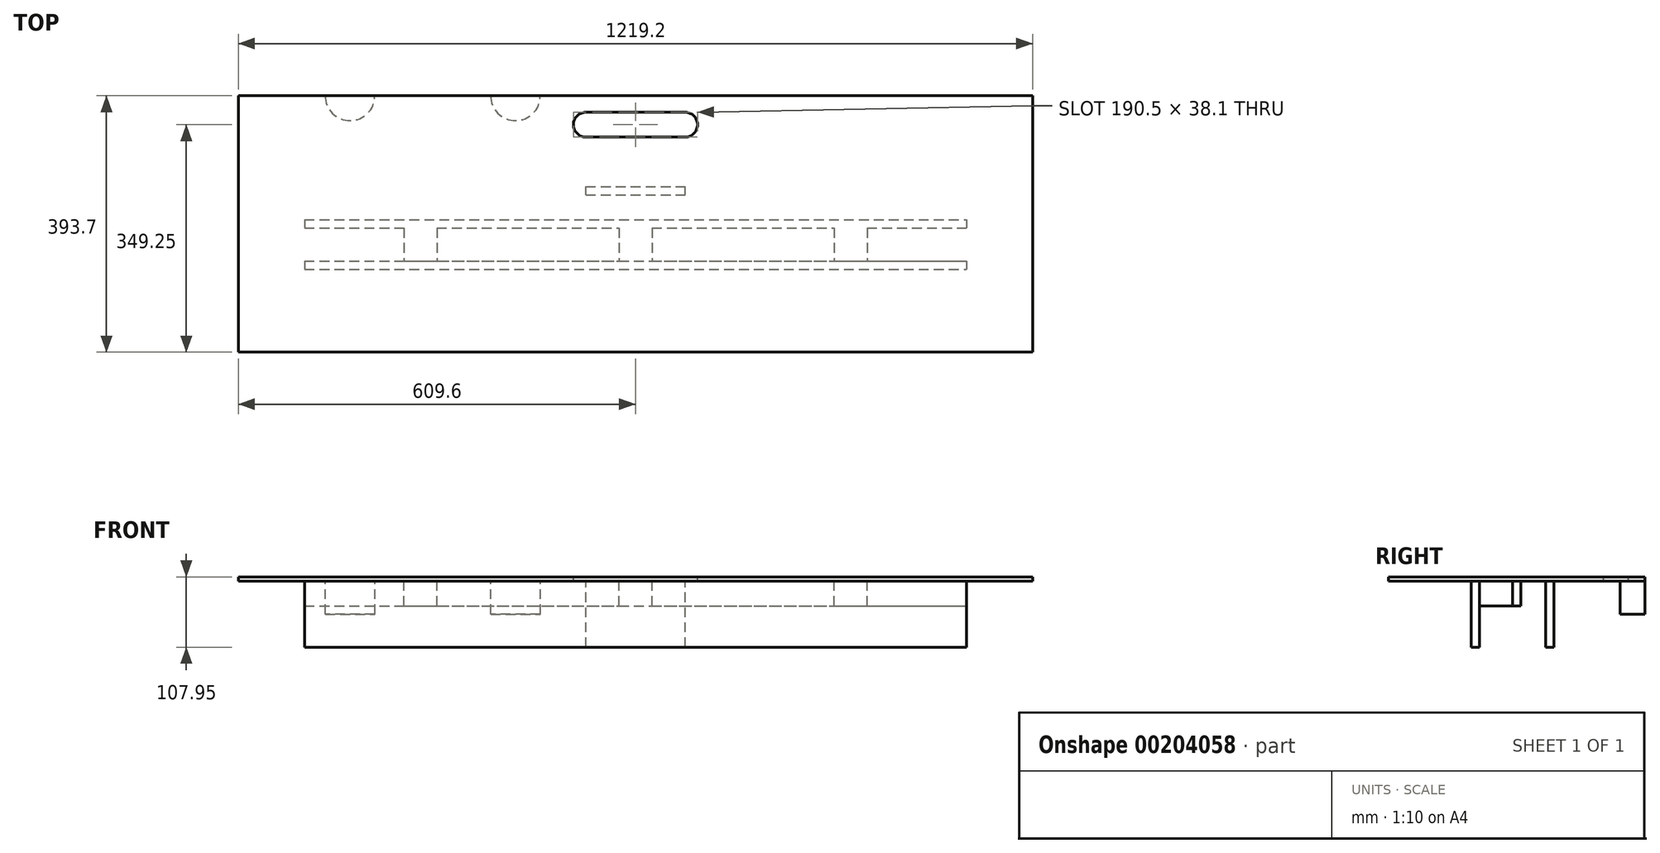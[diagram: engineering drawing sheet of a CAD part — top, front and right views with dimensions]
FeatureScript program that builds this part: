
annotation { "Feature Type Name" : "Feature", "Feature Type Description" : "" }
export const myFeature = defineFeature(function(context is Context, id is Id, definition is map)
    precondition{}
    {
        {
            var Q0;
            Q0=qCreatedBy(makeId("Top.planeOp"),FACE);
            var sketch = newSketch(context, id + "F0", { "sketchPlane" : qUnion([Q0])});
            skLineSegment(sketch, "E0.bottom", {"start": v(0, 0) * mm, "end": v(1219.2, 0) * mm});
            skLineSegment(sketch, "E0.top", {"start": v(0, 393.7) * mm, "end": v(1219.2, 393.7) * mm});
            skLineSegment(sketch, "E0.left", {"start": v(0, 0) * mm, "end": v(0, 393.7) * mm});
            skLineSegment(sketch, "E0.right", {"start": v(1219.2, 0) * mm, "end": v(1219.2, 393.7) * mm});
            skSolve(sketch);
        }
        {
            var Q0;
            Q0=makeQuery(id+"F0.imprint","IMPRINT",FACE,{"disambiguationData":[TD([[makeQuery(id+"F0.imprint","IMPRINT",EDGE,{"derivedFrom":sQuery(id+"F0.wireOp",EDGE,"E0.bottom")}),1.0]])]});
            extrude(context, id + "F1", {"entities" : qUnion([Q0]), "depth" : 6.35 * mm});
        }
        {
            var Q0;
            Q0=makeQuery(id+"F1.opExtrude","CAP_FACE",FACE,{"disambiguationData":[OSD([sQuery(id+"F0.wireOp",EDGE,"E0.bottom"),sQuery(id+"F0.wireOp",EDGE,"E0.top"),sQuery(id+"F0.wireOp",EDGE,"E0.left"),sQuery(id+"F0.wireOp",EDGE,"E0.right")])],"isStart":false});
            var sketch = newSketch(context, id + "F2", { "sketchPlane" : qUnion([Q0])});
            skLineSegment(sketch, "E1", {"start": v(533.4, 349.25) * mm, "end": v(685.8, 349.25) * mm});
            skLineSegment(sketch, "E2.0.0", {"start": v(0, 393.7) * mm, "end": v(0, 0) * mm});
            skLineSegment(sketch, "E2.0.1", {"start": v(0, 0) * mm, "end": v(1219.2, 0) * mm});
            skLineSegment(sketch, "E2.0.2", {"start": v(1219.2, 0) * mm, "end": v(1219.2, 393.7) * mm});
            skLineSegment(sketch, "E2.0.3", {"start": v(1219.2, 393.7) * mm, "end": v(0, 393.7) * mm});
            skLineSegment(sketch, "E3", {"start": v(609.6, 393.7) * mm, "end": v(609.6, 0) * mm, "construction": true});
            skCircle(sketch, "E4", {"center": v(533.4, 349.25) * mm, "radius": 19.05 * mm});
            skCircle(sketch, "E5", {"center": v(685.8, 349.25) * mm, "radius": 19.05 * mm});
            skLineSegment(sketch, "E6", {"start": v(533.4, 368.3) * mm, "end": v(685.8, 368.3) * mm});
            skLineSegment(sketch, "E7", {"start": v(685.8, 330.2) * mm, "end": v(533.4, 330.2) * mm});
            skSolve(sketch);
        }
        {
            var Q0;
            {var subQ0=sQuery(id+"F2.wireOp",EDGE,"E4");var subQ1=makeQuery(id+"F2.imprint","INTERSECT",VERTEX,{"derivedFrom":[subQ0,sQuery(id+"F2.wireOp",EDGE,"E6")]});Q0=makeQuery(id+"F2.imprint","IMPRINT",FACE,{"disambiguationData":[TD([[makeQuery(id+"F2.imprint","IMPRINT",EDGE,{"disambiguationData":[TD([[subQ1,1.0]])],"derivedFrom":subQ0}),1.0]])]});}
            var Q1;
            {var subQ5=sQuery(id+"F2.wireOp",EDGE,"E6");Q1=makeQuery(id+"F2.imprint","IMPRINT",FACE,{"disambiguationData":[TD([[makeQuery(id+"F2.imprint","IMPRINT",EDGE,{"derivedFrom":subQ5}),-1.0]])]});}
            var Q2;
            {var subQ5=sQuery(id+"F2.wireOp",EDGE,"E7");Q2=makeQuery(id+"F2.imprint","IMPRINT",FACE,{"disambiguationData":[TD([[makeQuery(id+"F2.imprint","IMPRINT",EDGE,{"derivedFrom":subQ5}),-1.0]])]});}
            var Q3;
            {var subQ0=sQuery(id+"F2.wireOp",EDGE,"E5");var subQ1=makeQuery(id+"F2.imprint","INTERSECT",VERTEX,{"derivedFrom":[subQ0,sQuery(id+"F2.wireOp",EDGE,"E6")]});Q3=makeQuery(id+"F2.imprint","IMPRINT",FACE,{"disambiguationData":[TD([[makeQuery(id+"F2.imprint","IMPRINT",EDGE,{"disambiguationData":[TD([[subQ1,-1.0]])],"derivedFrom":subQ0}),1.0]])]});}
            extrude(context, id + "F3", {"entities" : qUnion([Q0, Q1, Q2, Q3]), "operationType" : NewBodyOperationType.REMOVE, "endBound" : BoundingType.THROUGH_ALL, "oppositeDirection" : true, "depth" : 25.4 * mm});
        }
        {
            var Q0;
            Q0=makeQuery(id+"F1.opExtrude","CAP_FACE",FACE,{"disambiguationData":[OSD([sQuery(id+"F0.wireOp",EDGE,"E0.bottom"),sQuery(id+"F0.wireOp",EDGE,"E0.top"),sQuery(id+"F0.wireOp",EDGE,"E0.left"),sQuery(id+"F0.wireOp",EDGE,"E0.right")])],"isStart":true});
            var sketch = newSketch(context, id + "F4", { "sketchPlane" : qUnion([Q0])});
            skLineSegment(sketch, "E8.0.0", {"start": v(0, 0) * mm, "end": v(0, -393.7) * mm});
            skLineSegment(sketch, "E8.0.1", {"start": v(0, -393.7) * mm, "end": v(1219.2, -393.7) * mm});
            skLineSegment(sketch, "E8.0.2", {"start": v(1219.2, -393.7) * mm, "end": v(1219.2, 0) * mm});
            skLineSegment(sketch, "E8.0.3", {"start": v(1219.2, 0) * mm, "end": v(0, 0) * mm});
            skLineSegment(sketch, "E9", {"start": v(609.6, -393.7) * mm, "end": v(609.6, 0) * mm, "construction": true});
            skLineSegment(sketch, "E10.bottom", {"start": v(533.4, -241.3) * mm, "end": v(685.8, -241.3) * mm});
            skLineSegment(sketch, "E10.top", {"start": v(533.4, -254) * mm, "end": v(685.8, -254) * mm});
            skLineSegment(sketch, "E10.left", {"start": v(533.4, -241.3) * mm, "end": v(533.4, -254) * mm});
            skLineSegment(sketch, "E10.right", {"start": v(685.8, -241.3) * mm, "end": v(685.8, -254) * mm});
            skSolve(sketch);
        }
        {
            var Q0;
            Q0=makeQuery(id+"F4.imprint","IMPRINT",FACE,{"disambiguationData":[TD([[makeQuery(id+"F4.imprint","IMPRINT",EDGE,{"derivedFrom":sQuery(id+"F4.wireOp",EDGE,"E10.bottom")}),-1.0]])]});
            extrude(context, id + "F5", {"entities" : qUnion([Q0]), "operationType" : NewBodyOperationType.ADD, "depth" : 101.6 * mm});
        }
        {
            var Q0;
            Q0=makeQuery(id+"F5.opExtrude","SWEPT_FACE",FACE,{"disambiguationData":[OSD([sQuery(id+"F4.wireOp",EDGE,"E10.bottom")])]});
            var sketch = newSketch(context, id + "F6", { "sketchPlane" : qUnion([Q0])});
            skLineSegment(sketch, "E11.0.0", {"start": v(685.8, 0) * mm, "end": v(533.4, 0) * mm});
            skLineSegment(sketch, "E11.0.1", {"start": v(533.4, 0) * mm, "end": v(533.4, -101.6) * mm});
            skLineSegment(sketch, "E11.0.2", {"start": v(533.4, -101.6) * mm, "end": v(685.8, -101.6) * mm});
            skLineSegment(sketch, "E11.0.3", {"start": v(685.8, -101.6) * mm, "end": v(685.8, 0) * mm});
            skLineSegment(sketch, "E12", {"start": v(533.4, -57.15) * mm, "end": v(685.8, -57.15) * mm});
            skSolve(sketch);
        }
        {
            var Q0;
            Q0=makeQuery(id+"F1.opExtrude","CAP_FACE",FACE,{"disambiguationData":[OSD([sQuery(id+"F0.wireOp",EDGE,"E0.bottom"),sQuery(id+"F0.wireOp",EDGE,"E0.top"),sQuery(id+"F0.wireOp",EDGE,"E0.left"),sQuery(id+"F0.wireOp",EDGE,"E0.right")])],"isStart":true});
            var sketch = newSketch(context, id + "F7", { "sketchPlane" : qUnion([Q0])});
            skCircle(sketch, "E13", {"center": v(425.45, -393.7) * mm, "radius": 38.1 * mm});
            skCircle(sketch, "E14", {"center": v(171.45, -393.7) * mm, "radius": 38.1 * mm});
            skArc(sketch, "E15.0", {"start": v(533.4, -368.3) * mm, "mid": v(514.35, -349.25) * mm, "end": v(533.4, -330.2) * mm});
            skLineSegment(sketch, "E16", {"start": v(609.6, -393.7) * mm, "end": v(609.6, 0) * mm, "construction": true});
            skCircle(sketch, "E17.MirrorC", {"center": v(793.75, -393.7) * mm, "radius": 38.1 * mm});
            skCircle(sketch, "E18.MirrorC", {"center": v(1047.75, -393.7) * mm, "radius": 38.1 * mm});
            skSolve(sketch);
        }
        {
            var Q0;
            {var subQ0=sQuery(id+"F7.wireOp",EDGE,"E14");var subQ1=makeQuery(id+"F1.opExtrude","CAP_EDGE",EDGE,{"disambiguationData":[OSD([sQuery(id+"F0.wireOp",EDGE,"E0.top")])],"isStart":true});var subQ2=makeQuery(id+"F7.imprint","INTERSECT",VERTEX,{"disambiguationData":[OD(0.0)],"derivedFrom":[subQ1,subQ0]});Q0=makeQuery(id+"F7.imprint","IMPRINT",FACE,{"disambiguationData":[TD([[makeQuery(id+"F7.imprint","IMPRINT",EDGE,{"disambiguationData":[TD([[subQ2,1.0]])],"derivedFrom":subQ0}),1.0]])]});}
            var Q1;
            {var subQ0=sQuery(id+"F7.wireOp",EDGE,"E13");var subQ1=makeQuery(id+"F1.opExtrude","CAP_EDGE",EDGE,{"disambiguationData":[OSD([sQuery(id+"F0.wireOp",EDGE,"E0.top")])],"isStart":true});var subQ2=makeQuery(id+"F7.imprint","INTERSECT",VERTEX,{"disambiguationData":[OD(0.0)],"derivedFrom":[subQ1,subQ0]});Q1=makeQuery(id+"F7.imprint","IMPRINT",FACE,{"disambiguationData":[TD([[makeQuery(id+"F7.imprint","IMPRINT",EDGE,{"disambiguationData":[TD([[subQ2,1.0]])],"derivedFrom":subQ0}),1.0]])]});}
            var Q2;
            {var subQ0=sQuery(id+"F7.wireOp",EDGE,"E17.MirrorC");var subQ1=makeQuery(id+"F1.opExtrude","CAP_EDGE",EDGE,{"disambiguationData":[OSD([sQuery(id+"F0.wireOp",EDGE,"E0.top")])],"isStart":true});var subQ2=makeQuery(id+"F7.imprint","INTERSECT",VERTEX,{"disambiguationData":[OD(0.0)],"derivedFrom":[subQ1,subQ0]});Q2=makeQuery(id+"F7.imprint","IMPRINT",FACE,{"disambiguationData":[TD([[makeQuery(id+"F7.imprint","IMPRINT",EDGE,{"disambiguationData":[TD([[subQ2,1.0]])],"derivedFrom":subQ0}),-1.0]])]});}
            var Q3;
            {var subQ0=sQuery(id+"F7.wireOp",EDGE,"E18.MirrorC");var subQ1=makeQuery(id+"F1.opExtrude","CAP_EDGE",EDGE,{"disambiguationData":[OSD([sQuery(id+"F0.wireOp",EDGE,"E0.top")])],"isStart":true});var subQ2=makeQuery(id+"F7.imprint","INTERSECT",VERTEX,{"disambiguationData":[OD(0.0)],"derivedFrom":[subQ1,subQ0]});Q3=makeQuery(id+"F7.imprint","IMPRINT",FACE,{"disambiguationData":[TD([[makeQuery(id+"F7.imprint","IMPRINT",EDGE,{"disambiguationData":[TD([[subQ2,1.0]])],"derivedFrom":subQ0}),-1.0]])]});}
            extrude(context, id + "F8", {"entities" : qUnion([Q0, Q1, Q2, Q3]), "operationType" : NewBodyOperationType.ADD, "depth" : 50.8 * mm});
        }
        {
            var Q0;
            Q0=makeQuery(id+"F1.opExtrude","CAP_FACE",FACE,{"disambiguationData":[OSD([sQuery(id+"F0.wireOp",EDGE,"E0.bottom"),sQuery(id+"F0.wireOp",EDGE,"E0.top"),sQuery(id+"F0.wireOp",EDGE,"E0.left"),sQuery(id+"F0.wireOp",EDGE,"E0.right")])],"isStart":true});
            var sketch = newSketch(context, id + "F9", { "sketchPlane" : qUnion([Q0])});
            skLineSegment(sketch, "E19", {"start": v(0, -190.5) * mm, "end": v(1219.2, -190.5) * mm});
            skLineSegment(sketch, "E20", {"start": v(0, -203.2) * mm, "end": v(1219.2, -203.2) * mm});
            skLineSegment(sketch, "E21", {"start": v(0, -127) * mm, "end": v(1219.2, -127) * mm});
            skLineSegment(sketch, "E22", {"start": v(0, -139.7) * mm, "end": v(1219.2, -139.7) * mm});
            skLineSegment(sketch, "E23.0.0", {"start": v(685.8, -254) * mm, "end": v(685.8, -209.55) * mm});
            skLineSegment(sketch, "E23.0.1", {"start": v(685.8, -209.55) * mm, "end": v(533.4, -209.55) * mm});
            skLineSegment(sketch, "E23.0.2", {"start": v(533.4, -209.55) * mm, "end": v(533.4, -254) * mm});
            skLineSegment(sketch, "E23.0.3", {"start": v(533.4, -254) * mm, "end": v(685.8, -254) * mm});
            skLineSegment(sketch, "E24", {"start": v(254, -190.5) * mm, "end": v(254, -139.7) * mm});
            skLineSegment(sketch, "E25", {"start": v(304.8, -190.5) * mm, "end": v(304.8, -139.7) * mm});
            skLineSegment(sketch, "E26", {"start": v(609.6, -190.5) * mm, "end": v(609.6, -139.7) * mm, "construction": true});
            skLineSegment(sketch, "E27", {"start": v(635, -190.5) * mm, "end": v(635, -139.7) * mm});
            skLineSegment(sketch, "E28", {"start": v(584.2, -190.5) * mm, "end": v(584.2, -139.7) * mm});
            skLineSegment(sketch, "E29", {"start": v(965.2, -190.5) * mm, "end": v(965.2, -139.7) * mm});
            skLineSegment(sketch, "E30", {"start": v(914.4, -190.5) * mm, "end": v(914.4, -139.7) * mm});
            skLineSegment(sketch, "E31", {"start": v(101.6, -203.2) * mm, "end": v(101.6, -127) * mm});
            skLineSegment(sketch, "E32", {"start": v(1117.6, -203.2) * mm, "end": v(1117.6, -127) * mm});
            skSolve(sketch);
        }
        {
            var Q0;
            {var subQ0=sQuery(id+"F9.wireOp",EDGE,"E19");Q0=makeQuery(id+"F9.imprint","IMPRINT",FACE,{"disambiguationData":[TD([[makeQuery(id+"F9.imprint","IMPRINT",EDGE,{"derivedFrom":subQ0}),-1.0]])]});}
            extrude(context, id + "F10", {"entities" : qUnion([Q0]), "operationType" : NewBodyOperationType.ADD, "depth" : 38.1 * mm});
        }
        {
            var Q0;
            {var subQ4=sQuery(id+"F9.wireOp",EDGE,"E31");var subQ8=sQuery(id+"F9.wireOp",EDGE,"E21");var subQ9=makeQuery(id+"F9.imprint","INTERSECT",VERTEX,{"derivedFrom":[subQ8,subQ4]});Q0=makeQuery(id+"F9.imprint","IMPRINT",FACE,{"disambiguationData":[TD([[makeQuery(id+"F9.imprint","IMPRINT",EDGE,{"disambiguationData":[TD([[subQ9,-1.0]])],"derivedFrom":subQ8}),-1.0]])]});}
            extrude(context, id + "F11", {"entities" : qUnion([Q0]), "operationType" : NewBodyOperationType.ADD, "depth" : 101.6 * mm});
        }
        {
            var Q0;
            {var subQ0=sQuery(id+"F9.wireOp",EDGE,"E24");Q0=makeQuery(id+"F9.imprint","IMPRINT",FACE,{"disambiguationData":[TD([[makeQuery(id+"F9.imprint","IMPRINT",EDGE,{"derivedFrom":subQ0}),-1.0]])]});}
            var Q1;
            {var subQ0=sQuery(id+"F9.wireOp",EDGE,"E27");Q1=makeQuery(id+"F9.imprint","IMPRINT",FACE,{"disambiguationData":[TD([[makeQuery(id+"F9.imprint","IMPRINT",EDGE,{"derivedFrom":subQ0}),1.0]])]});}
            var Q2;
            {var subQ0=sQuery(id+"F9.wireOp",EDGE,"E29");Q2=makeQuery(id+"F9.imprint","IMPRINT",FACE,{"disambiguationData":[TD([[makeQuery(id+"F9.imprint","IMPRINT",EDGE,{"derivedFrom":subQ0}),1.0]])]});}
            var Q3;
            Q3=makeQuery(id+"F10.opExtrude","CAP_FACE",FACE,{"disambiguationData":[OSD([sQuery(id+"F0.wireOp",EDGE,"E0.left"),sQuery(id+"F0.wireOp",EDGE,"E0.right"),sQuery(id+"F9.wireOp",EDGE,"E19"),sQuery(id+"F9.wireOp",EDGE,"E20")])],"isStart":false});
            extrude(context, id + "F12", {"entities" : qUnion([Q0, Q1, Q2]), "operationType" : NewBodyOperationType.ADD, "endBound" : BoundingType.UP_TO_SURFACE, "endBoundEntityFace" : qUnion([Q3]), "depth" : 25.4 * mm});
        }
    });
